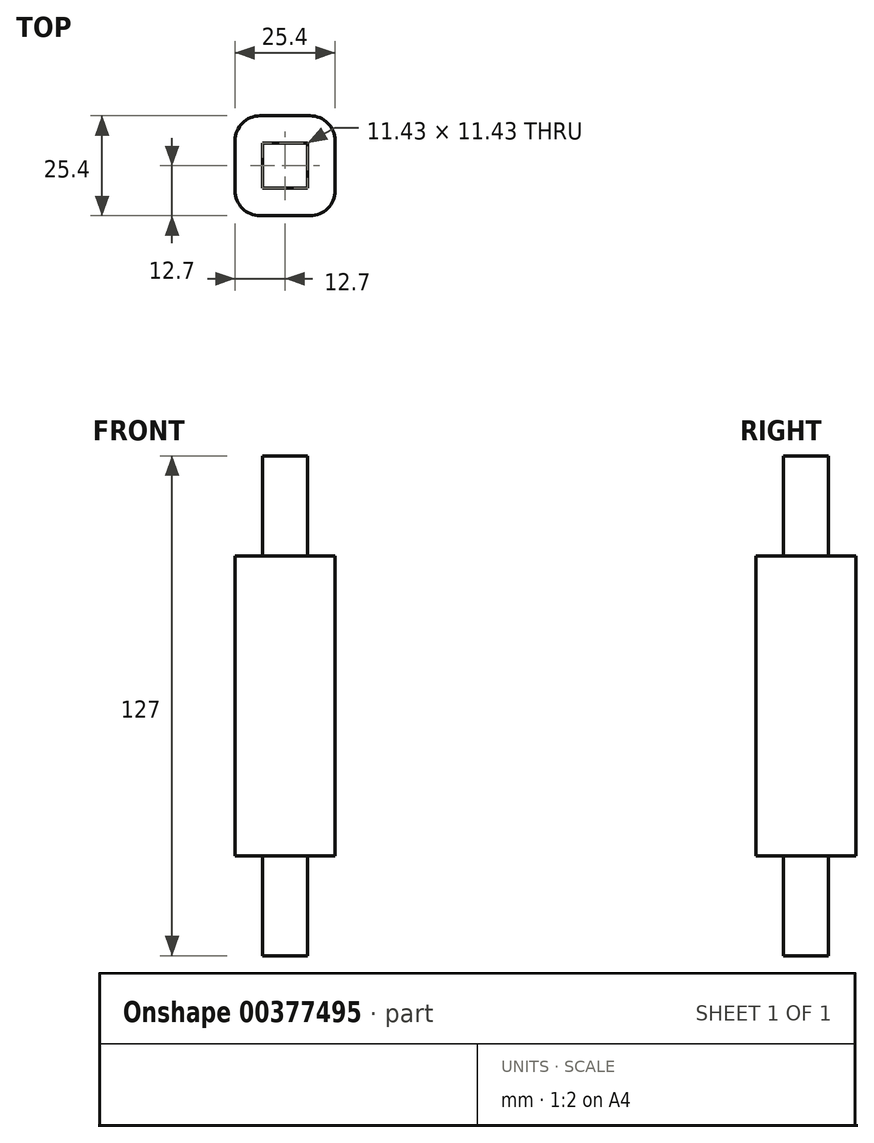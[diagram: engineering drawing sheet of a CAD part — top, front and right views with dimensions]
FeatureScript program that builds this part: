
annotation { "Feature Type Name" : "Feature", "Feature Type Description" : "" }
export const myFeature = defineFeature(function(context is Context, id is Id, definition is map)
    precondition{}
    {
        {
            var Q0;
            Q0=qCreatedBy(makeId("Front.planeOp"),FACE);
            var sketch = newSketch(context, id + "F0", { "sketchPlane" : qUnion([Q0])});
            skLineSegment(sketch, "E0", {"start": v(0, 0) * mm, "end": v(-12.7, 0) * mm});
            skLineSegment(sketch, "E1", {"start": v(-12.7, 0) * mm, "end": v(-12.7, 38.1) * mm});
            skLineSegment(sketch, "E2", {"start": v(-12.7, 38.1) * mm, "end": v(0, 38.1) * mm});
            skLineSegment(sketch, "E3.MirrorCS", {"start": v(12.7, 38.1) * mm, "end": v(0, 38.1) * mm});
            skLineSegment(sketch, "E4.MirrorCS", {"start": v(12.7, 0) * mm, "end": v(12.7, 38.1) * mm});
            skLineSegment(sketch, "E5.MirrorCS", {"start": v(0, 0) * mm, "end": v(12.7, 0) * mm});
            skSolve(sketch);
        }
        {
            var Q0;
            Q0 = qSketchRegion(id + "F0", true);
            extrude(context, id + "F1", {"entities" : qUnion([Q0]), "depth" : 25.4 * mm});
        }
        {
            var Q0;
            Q0=makeQuery(id+"F1.opExtrude","SWEPT_FACE",FACE,{"disambiguationData":[OSD([sQuery(id+"F0.wireOp",EDGE,"E2"),sQuery(id+"F0.wireOp",EDGE,"E3.MirrorCS")])]});
            var sketch = newSketch(context, id + "F2", { "sketchPlane" : qUnion([Q0])});
            skLineSegment(sketch, "E6", {"start": v(0, 0) * mm, "end": v(0, -25.4) * mm});
            skLineSegment(sketch, "E7", {"start": v(0, -25.4) * mm, "end": v(0, -12.7) * mm});
            skLineSegment(sketch, "E8.bottom", {"start": v(5.72, -18.41) * mm, "end": v(-5.71, -18.41) * mm});
            skLineSegment(sketch, "E8.top", {"start": v(5.72, -6.99) * mm, "end": v(-5.71, -6.99) * mm});
            skLineSegment(sketch, "E8.left", {"start": v(5.72, -18.41) * mm, "end": v(5.72, -6.99) * mm});
            skLineSegment(sketch, "E8.right", {"start": v(-5.71, -18.41) * mm, "end": v(-5.71, -6.99) * mm});
            skPoint(sketch, "E8.middle", {"position": v(0, -12.7) * mm});
            skSolve(sketch);
        }
        {
            var Q0;
            Q0 = qSketchRegion(id + "F2", true);
            extrude(context, id + "F3", {"entities" : qUnion([Q0]), "operationType" : NewBodyOperationType.ADD, "depth" : 25.4 * mm});
        }
        {
            var Q0;
            Q0=makeQuery(id+"F1.opExtrude","SWEPT_BODY",BODY,{"disambiguationData":[OSD([sQuery(id+"F0.wireOp",EDGE,"E0"),sQuery(id+"F0.wireOp",EDGE,"E1"),sQuery(id+"F0.wireOp",EDGE,"E2"),sQuery(id+"F0.wireOp",EDGE,"E3.MirrorCS"),sQuery(id+"F0.wireOp",EDGE,"E4.MirrorCS"),sQuery(id+"F0.wireOp",EDGE,"E5.MirrorCS")])]});
            var Q1;
            Q1=qCreatedBy(makeId("Top.planeOp"),FACE);
            mirror(context, id + "F4", {"operationType" : NewBodyOperationType.ADD, "entities" : qUnion([Q0]), "mirrorPlane" : qUnion([Q1])});
        }
        {
            var Q0;
            {var subQ0=makeQuery(id+"F1.opExtrude","CAP_EDGE",EDGE,{"disambiguationData":[OSD([sQuery(id+"F0.wireOp",EDGE,"E4.MirrorCS")])],"isStart":true});Q0=makeQuery(id+"F4.boolean.opBoolean","MERGE",EDGE,{"derivedFrom":[subQ0,makeQuery(id+"F4.opPattern","COPY",EDGE,{"derivedFrom":subQ0,"instanceName":"1"})]});}
            var Q1;
            {var subQ0=makeQuery(id+"F1.opExtrude","CAP_EDGE",EDGE,{"disambiguationData":[OSD([sQuery(id+"F0.wireOp",EDGE,"E4.MirrorCS")])],"isStart":false});Q1=makeQuery(id+"F4.boolean.opBoolean","MERGE",EDGE,{"derivedFrom":[subQ0,makeQuery(id+"F4.opPattern","COPY",EDGE,{"derivedFrom":subQ0,"instanceName":"1"})]});}
            var Q2;
            {var subQ0=makeQuery(id+"F1.opExtrude","CAP_EDGE",EDGE,{"disambiguationData":[OSD([sQuery(id+"F0.wireOp",EDGE,"E1")])],"isStart":true});Q2=makeQuery(id+"F4.boolean.opBoolean","MERGE",EDGE,{"derivedFrom":[subQ0,makeQuery(id+"F4.opPattern","COPY",EDGE,{"derivedFrom":subQ0,"instanceName":"1"})]});}
            var Q3;
            {var subQ0=makeQuery(id+"F1.opExtrude","CAP_EDGE",EDGE,{"disambiguationData":[OSD([sQuery(id+"F0.wireOp",EDGE,"E1")])],"isStart":false});Q3=makeQuery(id+"F4.boolean.opBoolean","MERGE",EDGE,{"derivedFrom":[subQ0,makeQuery(id+"F4.opPattern","COPY",EDGE,{"derivedFrom":subQ0,"instanceName":"1"})]});}
            fillet(context, id + "F5", {"entities" : qUnion([Q0, Q1, Q2, Q3]), "radius" : 6.35 * mm, "tangentPropagation" : true, "allowEdgeOverflow" : false});
        }
    });
